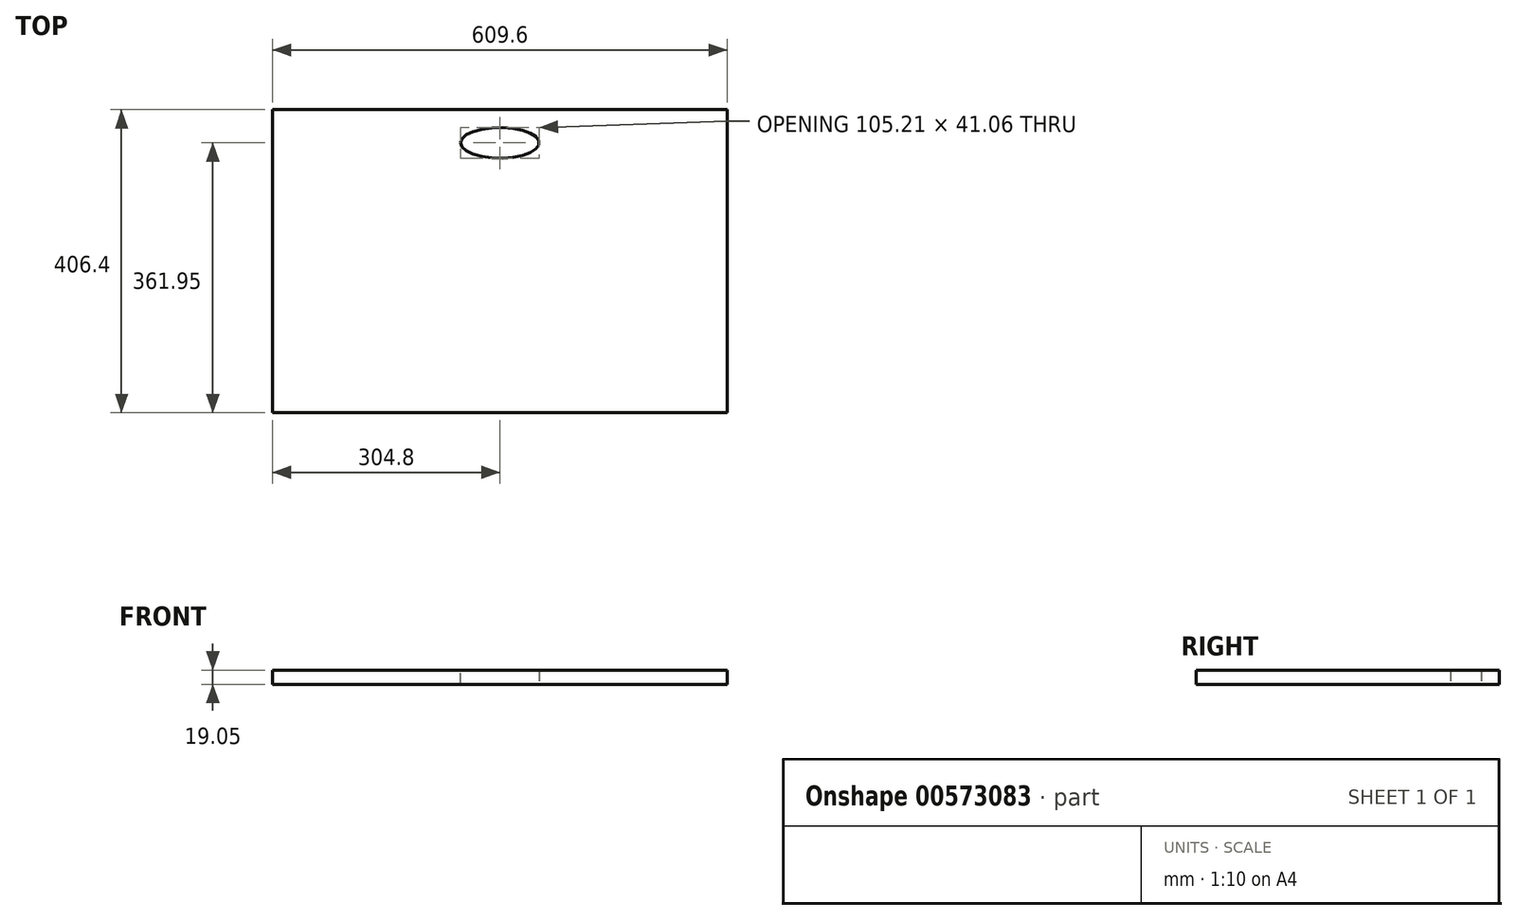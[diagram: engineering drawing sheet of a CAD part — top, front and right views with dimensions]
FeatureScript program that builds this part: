
annotation { "Feature Type Name" : "Feature", "Feature Type Description" : "" }
export const myFeature = defineFeature(function(context is Context, id is Id, definition is map)
    precondition{}
    {
        {
            var Q0;
            Q0=qCreatedBy(makeId("Top.planeOp"),FACE);
            var sketch = newSketch(context, id + "F0", { "sketchPlane" : qUnion([Q0])});
            skLineSegment(sketch, "E0.bottom", {"start": v(304.8, 203.2) * mm, "end": v(-304.8, 203.2) * mm});
            skLineSegment(sketch, "E0.top", {"start": v(304.8, -203.2) * mm, "end": v(-304.8, -203.2) * mm});
            skLineSegment(sketch, "E0.left", {"start": v(304.8, 203.2) * mm, "end": v(304.8, -203.2) * mm});
            skLineSegment(sketch, "E0.right", {"start": v(-304.8, 203.2) * mm, "end": v(-304.8, -203.2) * mm});
            skPoint(sketch, "E0.middle", {"position": v(0, 0) * mm});
            skSolve(sketch);
        }
        {
            var Q0;
            Q0=makeQuery(id+"F0.imprint","IMPRINT",FACE,{"disambiguationData":[TD([[makeQuery(id+"F0.imprint","IMPRINT",EDGE,{"derivedFrom":sQuery(id+"F0.wireOp",EDGE,"E0.bottom")}),1.0]])]});
            extrude(context, id + "F1", {"entities" : qUnion([Q0]), "depth" : 19.05 * mm, "offsetDistance" : 25.4 * mm});
        }
        {
            var Q0;
            Q0=makeQuery(id+"F1.opExtrude","CAP_FACE",FACE,{"disambiguationData":[OSD([sQuery(id+"F0.wireOp",EDGE,"E0.bottom"),sQuery(id+"F0.wireOp",EDGE,"E0.top"),sQuery(id+"F0.wireOp",EDGE,"E0.left"),sQuery(id+"F0.wireOp",EDGE,"E0.right")])],"isStart":false});
            var sketch = newSketch(context, id + "F2", { "sketchPlane" : qUnion([Q0])});
            skSolve(sketch);
        }
        {
            var Q0;
            Q0=makeQuery(id+"F2.imprint","IMPRINT",FACE,{"disambiguationData":[TD([[makeQuery(id+"F2.imprint","IMPRINT",EDGE,{"derivedFrom":makeQuery(id+"F1.opExtrude","CAP_EDGE",EDGE,{"disambiguationData":[OSD([sQuery(id+"F0.wireOp",EDGE,"E0.bottom")])],"isStart":false})}),1.0]])]});
            var sketch = newSketch(context, id + "F3", { "sketchPlane" : qUnion([Q0])});
            skEllipse(sketch, "E1", {"center": v(0, 158.75) * mm, "majorRadius": 52.6 * mm, "minorRadius": 20.53 * mm, "majorAxis": v(-1, 0)});
            skSolve(sketch);
        }
        {
            var Q0;
            Q0=makeQuery(id+"F3.imprint","IMPRINT",FACE,{"disambiguationData":[TD([[makeQuery(id+"F3.imprint","IMPRINT",EDGE,{"derivedFrom":sQuery(id+"F3.wireOp",EDGE,"E1")}),1.0]])]});
            extrude(context, id + "F4", {"entities" : qUnion([Q0]), "operationType" : NewBodyOperationType.REMOVE, "oppositeDirection" : true, "depth" : 25.4 * mm, "offsetDistance" : 25.4 * mm});
        }
    });
